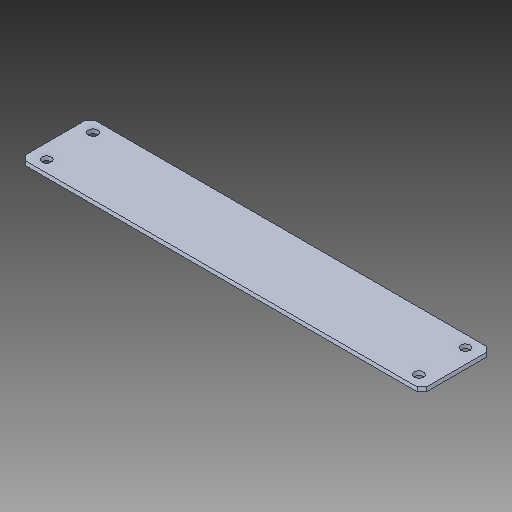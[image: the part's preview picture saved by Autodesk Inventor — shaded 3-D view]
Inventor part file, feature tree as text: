
AUTODESK INVENTOR PART (.ipt)
format: ipt  version: 2018.2 (Build 222227000, 227)  size: 88,576 bytes
history: native  units: in
note: dims shown in document units (in); Inventor stores cm internally (conversion verified against a paired STEP export)
features: chamfer x1
ambient origin geometry x8: Origin, YZ Plane, XZ Plane, XY Plane, X Axis, Y Axis, Z Axis, Center Point
bodies: Solid1 (feature_tree)
feature tree (1):
  chamfer  "Chamfer1"  [1 undecoded]
note: 1 required parameter value undecoded (feature->parameter linkage not recoverable at this tier; creation-order binding heuristic only, values carry confidence <= 0.55)
